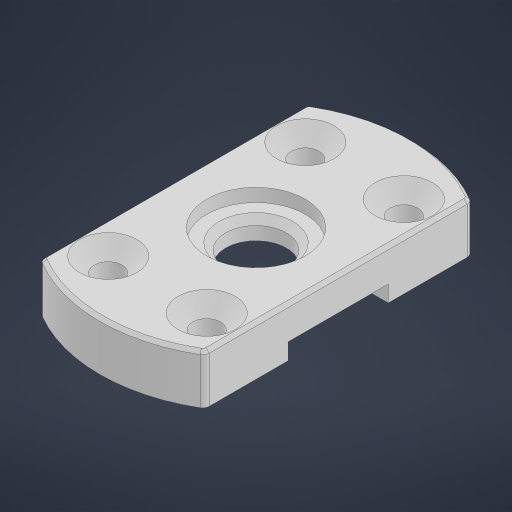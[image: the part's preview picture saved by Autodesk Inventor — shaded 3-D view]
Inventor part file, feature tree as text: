
AUTODESK INVENTOR PART (.ipt)
format: ipt  version: 2024.3 (Build 283343000, 343)  size: 243,712 bytes
history: native  units: mm
features: extrude x4, sketch x4, chamfer x2, hole x1, fillet x1, projected_geometry x1
ambient origin geometry x8: Origin, YZ Plane, XZ Plane, XY Plane, X Axis, Y Axis, Z Axis, Center Point
bodies: Body1 (feature_tree)
feature tree (13):
  extrude  "Extrusion2"  Depth=50.0mm
  sketch  "Sketch3"  dims[d5=15.0mm d6=0.0mm d7=30.5mm]
  extrude  "Extrusion3"  Depth=30.5mm
  extrude  "Extrusion4"  Depth=5.0mm
  extrude  "Extrusion5"  Depth=2.0mm
  chamfer  "Chamfer1"  Distance=4.0mm
  hole  "Hole1"  [1 undecoded]
  fillet  "Fillet1"  Radius=30.0mm
  chamfer  "Chamfer2"  Distance=60.0mm
  sketch  "Sketch2"  dims[d3=95.0mm d4=50.0mm]
  projected_geometry  "Projected Loop1"
  sketch  "Sketch4"  dims[d8=5.0mm d9=0.0mm d10=18.5mm]
  sketch  "Sketch5"  dims[d11=0.0mm d12=0.0mm d13=30.0mm d14=4.0mm d15=0.0mm d16=2.0mm d17=2.0mm d18=45.0deg d19=30.0mm d20=60.0mm d21=8.5mm d22=16.0mm d23=17.5mm d24=2.0mm d25=90.0deg d26=20.4mm d27=20.594885mm d28=1.0mm d29=2.0mm d30=45.0deg d31=2.0mm]
note: 1 required parameter value undecoded (feature->parameter linkage not recoverable at this tier; creation-order binding heuristic only, values carry confidence <= 0.55)
